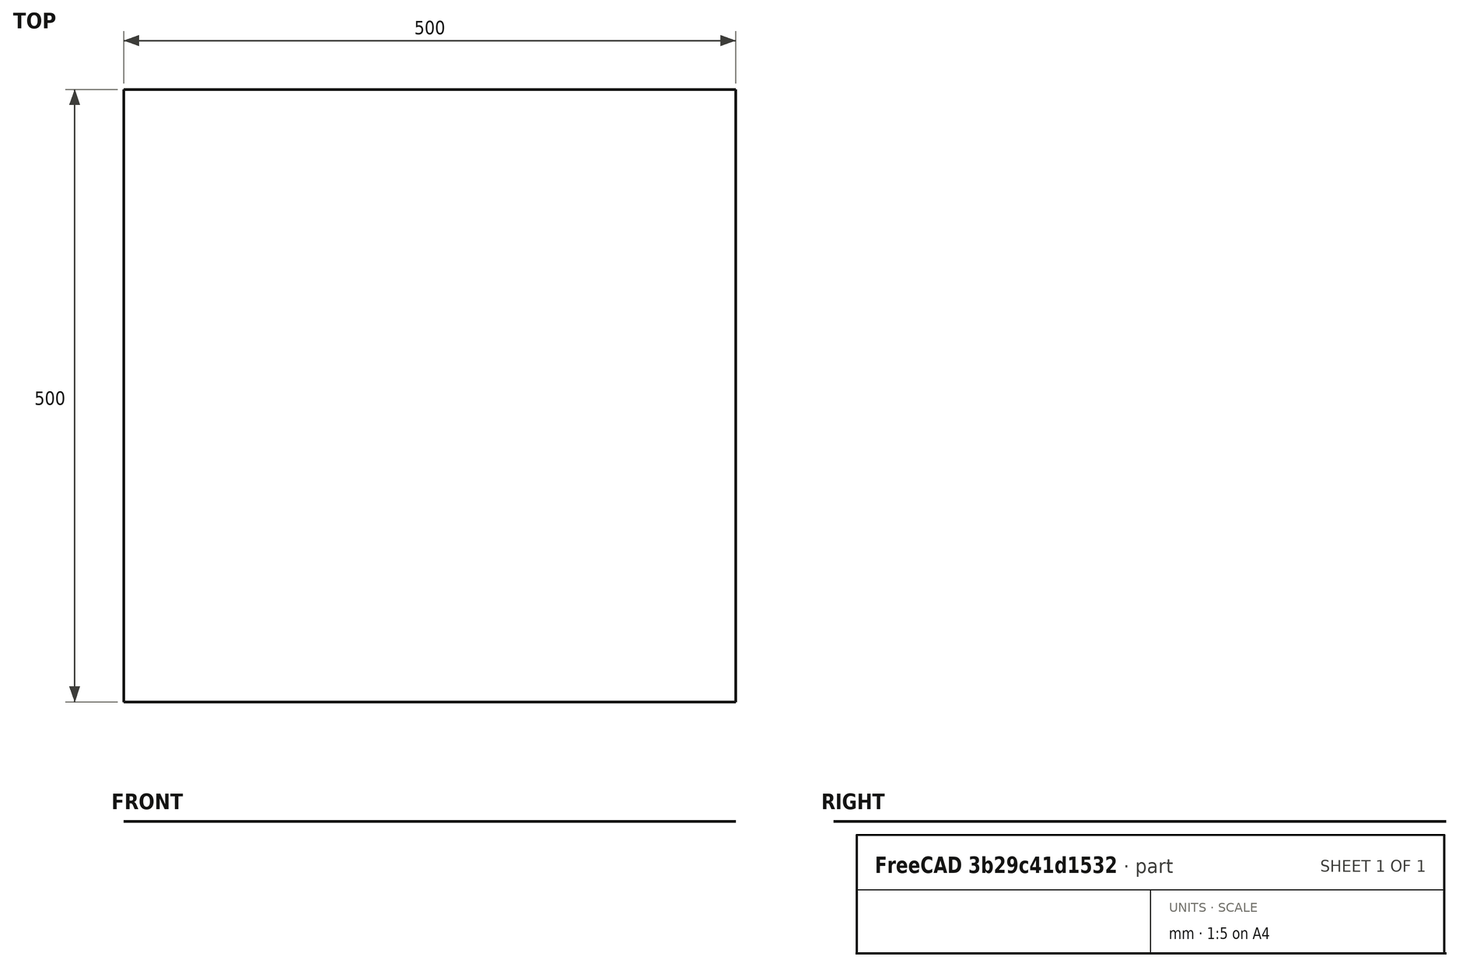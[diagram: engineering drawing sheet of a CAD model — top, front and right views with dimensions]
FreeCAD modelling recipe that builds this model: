
FCSTD DOCUMENT  (FreeCAD 0.19R16830 +1504 (Git))
Label: york_and_jaw
License: CreativeCommons Attribution
LicenseURL: http://creativecommons.org/licenses/by/4.0/
objects: App::FeaturePython×56, Part::FeaturePython×24, Part::Part2DObjectPython×6, Part::Polygon×1
note: 30 computed .brp shape members not serialized (recipe doc carries the construction recipe); baked Part::Feature solids carry a one-line shape summary decoded from their .brp

FEATURE [Part::FeaturePython] Workplane  # WARN: FeaturePython — macro-defined, semantics opaque (R4)
  Fixed = true
  Length = 500
  Placement = pos=(-250,-250,0) rot=(0,0,1;0rad)
  Width = 500
FEATURE [Part::Part2DObjectPython] Line  label="axis"  # Draft 2D object (typed FeaturePython)
  Area = 0
  ChamferSize = 0
  Closed = false
  End = (0,-300,0)
  FilletRadius = 0
  Length = 600
  MakeFace = false
  Placement = pos=(0,300,0) rot=(0,0,1;0rad)
  Points = (2) [(0,0,0),(0,-600,0)]
  Start = (0,300,0)
  Subdivisions = 0
FEATURE [Part::Part2DObjectPython] Wire  label="york"  # Draft 2D object (typed FeaturePython)
  Area = 0
  ChamferSize = 0
  Closed = false
  End = (60,-68.8578,0)
  FilletRadius = 0
  Length = 120
  MakeFace = false
  Placement = pos=(-60,0,0) rot=(0,0,1;0rad)
  Points = (3) [(1.42109e-14,-68.8578,0),(60,-68.8578,0),(120,-68.8578,0)]
  Start = (-60,-68.8578,0)
  Subdivisions = 0
FEATURE [Part::Part2DObjectPython] Wire001  label="cutter_jaw"  # Draft 2D object (typed FeaturePython)
  Area = 0
  ChamferSize = 0
  Closed = false
  End = (-142.748,-125.008,0)
  FilletRadius = 0
  Length = 272.324
  MakeFace = false
  Placement = pos=(-39.0753,157.598,0) rot=(0,0,1;0rad)
  Points = (3) [(-3.83776,-54.9816,0),(-20.9247,-226.456,0),(-103.673,-282.606,0)]
  Start = (-42.913,102.617,0)
  Subdivisions = 0
FEATURE [Part::Part2DObjectPython] Wire002  label="pressure_jaw"  # Draft 2D object (typed FeaturePython)
  Area = 0
  ChamferSize = 0
  Closed = false
  End = (142.748,-125.008,0)
  FilletRadius = 0
  Length = 274.62
  MakeFace = false
  Placement = pos=(41.1887,156.796,0) rot=(0,0,1;0rad)
  Points = (3) [(2.07288,-51.8375,0),(18.8113,-225.653,0),(101.559,-281.803,0)]
  Start = (43.2616,104.958,0)
  Subdivisions = 0
FEATURE [Part::Part2DObjectPython] Line001  label="cutter_link"  # Draft 2D object (typed FeaturePython)
  Area = 0
  ChamferSize = 0
  Closed = false
  End = (0,-185.407,0)
  FilletRadius = 0
  Length = 155
  MakeFace = false
  Placement = pos=(-185.958,-71.1542,0) rot=(0,0,1;0rad)
  Points = (2) [(43.2105,-53.8533,0),(185.958,-114.252,0)]
  Start = (-142.748,-125.008,0)
  Subdivisions = 0
FEATURE [Part::Part2DObjectPython] Line002  label="pressure_link"  # Draft 2D object (typed FeaturePython)
  Area = 0
  ChamferSize = 0
  Closed = false
  End = (142.748,-125.008,0)
  FilletRadius = 0
  Length = 155
  MakeFace = false
  Placement = pos=(19.9434,-112.883,0) rot=(0,0,1;0rad)
  Points = (2) [(-19.9434,-72.5236,0),(122.804,-12.1245,0)]
  Start = (7.1e-15,-185.407,0)
  Subdivisions = 0
FEATURE [Part::FeaturePython] Parts  # WARN: FeaturePython — macro-defined, semantics opaque (R4)
  Group = -> [Workplane,Line,Wire,Wire001,Wire002,Line001,Line002]
  GroupMode = 0
FEATURE [Part::Polygon] AsmTrace
  Close = false
  Nodes = (144) [(10.1055,126.573,0),(10.1055,126.573,0),(10.1616,126.566,0),(10.4758,126.524,0),(10.6524,126.463,0),(10.7929,126.386,0),(10.9479,126.292,0),+137 more]
FEATURE [Part::FeaturePython] Assembly  # WARN: FeaturePython — macro-defined, semantics opaque (R4)
  AutoRelax = true
  BuildShape = 0
  Freeze = false
  Group = -> [Constraints,Elements,Parts]
  GroupMode = 1
  SolverType = 1
  Verbose = false
  _SolverType = 1
  _Version = 1
FEATURE [App::FeaturePython] Constraints  # WARN: FeaturePython — macro-defined, semantics opaque (R4)
  Group = -> [Constraint,Constraint001,Constraint002,Constraint003,Constraint004,Constraint005,Constraint006,Constraint007,Constraint008,Constraint009,Constraint010,Constraint011,Constraint012,Constraint013,Constraint014,Constraint015,Constraint016,Constraint017,Constraint018,Constraint019,Constraint020]
  GroupMode = 1
  _Version = 1
FEATURE [App::FeaturePython] Elements  # WARN: FeaturePython — macro-defined, semantics opaque (R4)
  Group = -> [_Element,_Element001,_Element002,_Element003,_Element004,_Element005,_Element006,_Element007,_Element008,_Element009,_Element010,_Element011,_Element012,_Element013,_Element014,_Element015,_Element016,_Element017,_Element018,_Element019,_Element020]
  GroupMode = 1
FEATURE [App::FeaturePython] Constraint  label="SketchPlane"  # WARN: FeaturePython — macro-defined, semantics opaque (R4)
  ConstraintType = 28
  Disabled = false
  Group = -> [ElementLink]
  GroupMode = 1
  _ConstraintType = 38
  _Parent = -> Constraints
FEATURE [App::FeaturePython] ElementLink  label="_Element"  # link proxy (typed FeaturePython)
  LinkTransform = true
  LinkedObject = -> _Element
  _Parent = -> Constraint
FEATURE [Part::FeaturePython] _Element  # link proxy (typed FeaturePython)
  Detach = false
  LinkTransform = true
  LinkedObject = -> Workplane [Face1]
  _Parent = -> Elements
FEATURE [App::FeaturePython] Constraint001  label="axis Locked"  # WARN: FeaturePython — macro-defined, semantics opaque (R4)
  ConstraintType = 0
  Disabled = false
  Group = -> [ElementLink001]
  GroupMode = 1
  _ConstraintType = 0
  _Parent = -> Constraints
FEATURE [App::FeaturePython] ElementLink001  label="_Element001"  # link proxy (typed FeaturePython)
  LinkTransform = true
  LinkedObject = -> _Element001
  _Parent = -> Constraint001
FEATURE [Part::FeaturePython] _Element001  # link proxy (typed FeaturePython)
  Detach = false
  LinkTransform = true
  LinkedObject = -> Line [Edge1]
  _Parent = -> Elements
FEATURE [Part::FeaturePython] _Element002  # link proxy (typed FeaturePython)
  Detach = false
  LinkTransform = true
  LinkedObject = -> Wire [Vertex3]
  _Parent = -> Elements
FEATURE [Part::FeaturePython] _Element003  # link proxy (typed FeaturePython)
  Detach = false
  LinkTransform = true
  LinkedObject = -> Wire [Vertex1]
  _Parent = -> Elements
FEATURE [App::FeaturePython] Constraint002  label="york_on_axis"  # WARN: FeaturePython — macro-defined, semantics opaque (R4)
  ConstraintType = 11
  Disabled = false
  Group = -> [ElementLink002,ElementLink003]
  GroupMode = 1
  _ConstraintType = 4
  _Parent = -> Constraints
FEATURE [App::FeaturePython] ElementLink002  label="_Element004"  # link proxy (typed FeaturePython)
  LinkTransform = true
  LinkedObject = -> _Element004
  _Parent = -> Constraint002
FEATURE [Part::FeaturePython] _Element004  # link proxy (typed FeaturePython)
  Detach = false
  LinkTransform = true
  LinkedObject = -> Wire [Vertex2]
  _Parent = -> Elements
FEATURE [App::FeaturePython] ElementLink003  label="_Element001"  # link proxy (typed FeaturePython)
  LinkTransform = true
  LinkedObject = -> _Element001
  _Parent = -> Constraint002
FEATURE [App::FeaturePython] Constraint003  label="EqualLength"  # WARN: FeaturePython — macro-defined, semantics opaque (R4)
  ConstraintType = 30
  Disabled = false
  Group = -> [ElementLink004,ElementLink005]
  GroupMode = 1
  _ConstraintType = 9
  _Parent = -> Constraints
FEATURE [App::FeaturePython] ElementLink004  label="_Element005"  # link proxy (typed FeaturePython)
  LinkTransform = true
  LinkedObject = -> _Element005
  _Parent = -> Constraint003
FEATURE [Part::FeaturePython] _Element005  # link proxy (typed FeaturePython)
  Detach = false
  LinkTransform = true
  LinkedObject = -> Wire [Edge1]
  _Parent = -> Elements
FEATURE [App::FeaturePython] ElementLink005  label="_Element006"  # link proxy (typed FeaturePython)
  LinkTransform = true
  LinkedObject = -> _Element006
  _Parent = -> Constraint003
FEATURE [Part::FeaturePython] _Element006  # link proxy (typed FeaturePython)
  Detach = false
  LinkTransform = true
  LinkedObject = -> Wire [Edge2]
  _Parent = -> Elements
FEATURE [App::FeaturePython] Constraint004  label="LineLength"  # WARN: FeaturePython — macro-defined, semantics opaque (R4)
  ConstraintType = 29
  Disabled = false
  Group = -> [ElementLink006]
  GroupMode = 1
  Length = 60
  _ConstraintType = 34
  _Parent = -> Constraints
FEATURE [App::FeaturePython] ElementLink006  label="_Element005"  # link proxy (typed FeaturePython)
  LinkTransform = true
  LinkedObject = -> _Element005
  _Parent = -> Constraint004
FEATURE [App::FeaturePython] Constraint005  label="LineHorizontal"  # WARN: FeaturePython — macro-defined, semantics opaque (R4)
  ConstraintType = 25
  Disabled = false
  Group = -> [ElementLink007]
  GroupMode = 1
  _ConstraintType = 23
  _Parent = -> Constraints
FEATURE [App::FeaturePython] ElementLink007  label="_Element006"  # link proxy (typed FeaturePython)
  LinkTransform = true
  LinkedObject = -> _Element006
  _Parent = -> Constraint005
FEATURE [App::FeaturePython] Constraint006  label="LineHorizontal"  # WARN: FeaturePython — macro-defined, semantics opaque (R4)
  ConstraintType = 25
  Disabled = false
  Group = -> [ElementLink008]
  GroupMode = 1
  _ConstraintType = 23
  _Parent = -> Constraints
FEATURE [App::FeaturePython] ElementLink008  label="_Element005"  # link proxy (typed FeaturePython)
  LinkTransform = true
  LinkedObject = -> _Element005
  _Parent = -> Constraint006
FEATURE [App::FeaturePython] Constraint007  label="LineLength"  # WARN: FeaturePython — macro-defined, semantics opaque (R4)
  ConstraintType = 29
  Disabled = false
  Group = -> [ElementLink009]
  GroupMode = 1
  Length = 100
  _ConstraintType = 34
  _Parent = -> Constraints
FEATURE [App::FeaturePython] ElementLink009  label="_Element007"  # link proxy (typed FeaturePython)
  LinkTransform = true
  LinkedObject = -> _Element007
  _Parent = -> Constraint007
FEATURE [Part::FeaturePython] _Element007  # link proxy (typed FeaturePython)
  Detach = false
  LinkTransform = true
  LinkedObject = -> Wire001 [Edge2]
  _Parent = -> Elements
FEATURE [App::FeaturePython] Constraint008  label="EqualLength"  # WARN: FeaturePython — macro-defined, semantics opaque (R4)
  ConstraintType = 30
  Disabled = false
  Group = -> [ElementLink010,ElementLink011]
  GroupMode = 1
  _ConstraintType = 9
  _Parent = -> Constraints
FEATURE [App::FeaturePython] ElementLink010  label="_Element008"  # link proxy (typed FeaturePython)
  LinkTransform = true
  LinkedObject = -> _Element008
  _Parent = -> Constraint008
FEATURE [Part::FeaturePython] _Element008  # link proxy (typed FeaturePython)
  Detach = false
  LinkTransform = true
  LinkedObject = -> Wire002 [Edge2]
  _Parent = -> Elements
FEATURE [App::FeaturePython] ElementLink011  label="_Element007"  # link proxy (typed FeaturePython)
  LinkTransform = true
  LinkedObject = -> _Element007
  _Parent = -> Constraint008
FEATURE [App::FeaturePython] Constraint009  label="LineLength"  # WARN: FeaturePython — macro-defined, semantics opaque (R4)
  ConstraintType = 29
  Disabled = false
  Group = -> [ElementLink012]
  GroupMode = 1
  Length = 172.324
  _ConstraintType = 34
  _Parent = -> Constraints
FEATURE [App::FeaturePython] ElementLink012  label="_Element009"  # link proxy (typed FeaturePython)
  LinkTransform = true
  LinkedObject = -> _Element009
  _Parent = -> Constraint009
FEATURE [Part::FeaturePython] _Element009  # link proxy (typed FeaturePython)
  Detach = false
  LinkTransform = true
  LinkedObject = -> Wire001 [Edge1]
  _Parent = -> Elements
FEATURE [App::FeaturePython] Constraint010  label="LineLength"  # WARN: FeaturePython — macro-defined, semantics opaque (R4)
  ConstraintType = 29
  Disabled = false
  Group = -> [ElementLink013]
  GroupMode = 1
  Length = 174.62
  _ConstraintType = 34
  _Parent = -> Constraints
FEATURE [App::FeaturePython] ElementLink013  label="_Element010"  # link proxy (typed FeaturePython)
  LinkTransform = true
  LinkedObject = -> _Element010
  _Parent = -> Constraint010
FEATURE [Part::FeaturePython] _Element010  # link proxy (typed FeaturePython)
  Detach = false
  LinkTransform = true
  LinkedObject = -> Wire002 [Edge1]
  _Parent = -> Elements
FEATURE [App::FeaturePython] Constraint011  label="Angle"  # WARN: FeaturePython — macro-defined, semantics opaque (R4)
  Angle = 50.34
  ConstraintType = 7
  Disabled = false
  Group = -> [ElementLink014,ElementLink015]
  GroupMode = 1
  Supplement = false
  _ConstraintType = 27
  _Parent = -> Constraints
FEATURE [App::FeaturePython] ElementLink014  label="_Element010"  # link proxy (typed FeaturePython)
  LinkTransform = true
  LinkedObject = -> _Element010
  _Parent = -> Constraint011
FEATURE [App::FeaturePython] ElementLink015  label="_Element008"  # link proxy (typed FeaturePython)
  LinkTransform = true
  LinkedObject = -> _Element008
  _Parent = -> Constraint011
FEATURE [App::FeaturePython] Constraint012  label="Angle"  # WARN: FeaturePython — macro-defined, semantics opaque (R4)
  Angle = 50.15
  ConstraintType = 7
  Disabled = false
  Group = -> [ElementLink016,ElementLink017]
  GroupMode = 1
  Supplement = false
  _ConstraintType = 27
  _Parent = -> Constraints
FEATURE [App::FeaturePython] ElementLink016  label="_Element009"  # link proxy (typed FeaturePython)
  LinkTransform = true
  LinkedObject = -> _Element009
  _Parent = -> Constraint012
FEATURE [App::FeaturePython] ElementLink017  label="_Element007"  # link proxy (typed FeaturePython)
  LinkTransform = true
  LinkedObject = -> _Element007
  _Parent = -> Constraint012
FEATURE [App::FeaturePython] Constraint013  label="PointsCoincident"  # WARN: FeaturePython — macro-defined, semantics opaque (R4)
  ConstraintType = 9
  Disabled = false
  Group = -> [ElementLink018,ElementLink019]
  GroupMode = 1
  _ConstraintType = 1
  _Parent = -> Constraints
FEATURE [App::FeaturePython] ElementLink018  label="_Element011"  # link proxy (typed FeaturePython)
  LinkTransform = true
  LinkedObject = -> _Element011
  _Parent = -> Constraint013
FEATURE [Part::FeaturePython] _Element011  # link proxy (typed FeaturePython)
  Detach = false
  LinkTransform = true
  LinkedObject = -> Wire001 [Vertex2]
  _Parent = -> Elements
FEATURE [App::FeaturePython] ElementLink019  label="_Element003"  # link proxy (typed FeaturePython)
  LinkTransform = true
  LinkedObject = -> _Element003
  _Parent = -> Constraint013
FEATURE [App::FeaturePython] Constraint014  label="PointsCoincident"  # WARN: FeaturePython — macro-defined, semantics opaque (R4)
  ConstraintType = 9
  Disabled = false
  Group = -> [ElementLink020,ElementLink021]
  GroupMode = 1
  _ConstraintType = 1
  _Parent = -> Constraints
FEATURE [App::FeaturePython] ElementLink020  label="_Element012"  # link proxy (typed FeaturePython)
  LinkTransform = true
  LinkedObject = -> _Element012
  _Parent = -> Constraint014
FEATURE [Part::FeaturePython] _Element012  # link proxy (typed FeaturePython)
  Detach = false
  LinkTransform = true
  LinkedObject = -> Wire002 [Vertex2]
  _Parent = -> Elements
FEATURE [App::FeaturePython] ElementLink021  label="_Element002"  # link proxy (typed FeaturePython)
  LinkTransform = true
  LinkedObject = -> _Element002
  _Parent = -> Constraint014
FEATURE [App::FeaturePython] Constraint015  label="LineLength"  # WARN: FeaturePython — macro-defined, semantics opaque (R4)
  ConstraintType = 29
  Disabled = false
  Group = -> [ElementLink022]
  GroupMode = 1
  Length = 155
  _ConstraintType = 34
  _Parent = -> Constraints
FEATURE [App::FeaturePython] ElementLink022  label="_Element013"  # link proxy (typed FeaturePython)
  LinkTransform = true
  LinkedObject = -> _Element013
  _Parent = -> Constraint015
FEATURE [Part::FeaturePython] _Element013  # link proxy (typed FeaturePython)
  Detach = false
  LinkTransform = true
  LinkedObject = -> Line001 [Edge1]
  _Parent = -> Elements
FEATURE [App::FeaturePython] Constraint016  label="EqualLength"  # WARN: FeaturePython — macro-defined, semantics opaque (R4)
  ConstraintType = 30
  Disabled = false
  Group = -> [ElementLink023,ElementLink024]
  GroupMode = 1
  _ConstraintType = 9
  _Parent = -> Constraints
FEATURE [App::FeaturePython] ElementLink023  label="_Element013"  # link proxy (typed FeaturePython)
  LinkTransform = true
  LinkedObject = -> _Element013
  _Parent = -> Constraint016
FEATURE [App::FeaturePython] ElementLink024  label="_Element014"  # link proxy (typed FeaturePython)
  LinkTransform = true
  LinkedObject = -> _Element014
  _Parent = -> Constraint016
FEATURE [Part::FeaturePython] _Element014  # link proxy (typed FeaturePython)
  Detach = false
  LinkTransform = true
  LinkedObject = -> Line002 [Edge1]
  _Parent = -> Elements
FEATURE [App::FeaturePython] Constraint017  label="PointsCoincident"  # WARN: FeaturePython — macro-defined, semantics opaque (R4)
  ConstraintType = 9
  Disabled = false
  Group = -> [ElementLink025,ElementLink026]
  GroupMode = 1
  _ConstraintType = 1
  _Parent = -> Constraints
FEATURE [App::FeaturePython] ElementLink025  label="_Element015"  # link proxy (typed FeaturePython)
  LinkTransform = true
  LinkedObject = -> _Element015
  _Parent = -> Constraint017
FEATURE [Part::FeaturePython] _Element015  # link proxy (typed FeaturePython)
  Detach = false
  LinkTransform = true
  LinkedObject = -> Line001 [Vertex1]
  _Parent = -> Elements
FEATURE [App::FeaturePython] ElementLink026  label="_Element016"  # link proxy (typed FeaturePython)
  LinkTransform = true
  LinkedObject = -> _Element016
  _Parent = -> Constraint017
FEATURE [Part::FeaturePython] _Element016  # link proxy (typed FeaturePython)
  Detach = false
  LinkTransform = true
  LinkedObject = -> Wire001 [Vertex3]
  _Parent = -> Elements
FEATURE [App::FeaturePython] Constraint018  label="PointsCoincident"  # WARN: FeaturePython — macro-defined, semantics opaque (R4)
  ConstraintType = 9
  Disabled = false
  Group = -> [ElementLink027,ElementLink028]
  GroupMode = 1
  _ConstraintType = 1
  _Parent = -> Constraints
FEATURE [App::FeaturePython] ElementLink027  label="_Element017"  # link proxy (typed FeaturePython)
  LinkTransform = true
  LinkedObject = -> _Element017
  _Parent = -> Constraint018
FEATURE [Part::FeaturePython] _Element017  # link proxy (typed FeaturePython)
  Detach = false
  LinkTransform = true
  LinkedObject = -> Wire002 [Vertex3]
  _Parent = -> Elements
FEATURE [App::FeaturePython] ElementLink028  label="_Element018"  # link proxy (typed FeaturePython)
  LinkTransform = true
  LinkedObject = -> _Element018
  _Parent = -> Constraint018
FEATURE [Part::FeaturePython] _Element018  # link proxy (typed FeaturePython)
  Detach = false
  LinkTransform = true
  LinkedObject = -> Line002 [Vertex2]
  _Parent = -> Elements
FEATURE [App::FeaturePython] Constraint019  label="PointsCoincident"  # WARN: FeaturePython — macro-defined, semantics opaque (R4)
  ConstraintType = 9
  Disabled = false
  Group = -> [ElementLink029,ElementLink030]
  GroupMode = 1
  _ConstraintType = 1
  _Parent = -> Constraints
FEATURE [App::FeaturePython] ElementLink029  label="_Element019"  # link proxy (typed FeaturePython)
  LinkTransform = true
  LinkedObject = -> _Element019
  _Parent = -> Constraint019
FEATURE [Part::FeaturePython] _Element019  # link proxy (typed FeaturePython)
  Detach = false
  LinkTransform = true
  LinkedObject = -> Line001 [Vertex2]
  _Parent = -> Elements
FEATURE [App::FeaturePython] ElementLink030  label="_Element020"  # link proxy (typed FeaturePython)
  LinkTransform = true
  LinkedObject = -> _Element020
  _Parent = -> Constraint019
FEATURE [Part::FeaturePython] _Element020  # link proxy (typed FeaturePython)
  Detach = false
  LinkTransform = true
  LinkedObject = -> Line002 [Vertex1]
  _Parent = -> Elements
FEATURE [App::FeaturePython] Constraint020  label="PointOnLine"  # WARN: FeaturePython — macro-defined, semantics opaque (R4)
  ConstraintType = 11
  Disabled = false
  Group = -> [ElementLink031,ElementLink032]
  GroupMode = 1
  _ConstraintType = 4
  _Parent = -> Constraints
FEATURE [App::FeaturePython] ElementLink031  label="_Element019"  # link proxy (typed FeaturePython)
  LinkTransform = true
  LinkedObject = -> _Element019
  _Parent = -> Constraint020
FEATURE [App::FeaturePython] ElementLink032  label="_Element001"  # link proxy (typed FeaturePython)
  LinkTransform = true
  LinkedObject = -> _Element001
  _Parent = -> Constraint020
